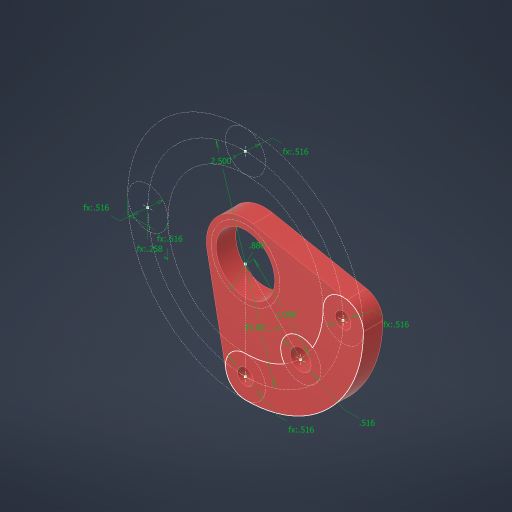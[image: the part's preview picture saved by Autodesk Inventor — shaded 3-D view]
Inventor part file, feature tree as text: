
AUTODESK INVENTOR PART (.ipt)
format: ipt  version: 2023.4 (Build 274418000, 418)  size: 238,080 bytes
history: native  units: in
note: dims shown in document units (in); Inventor stores cm internally (conversion verified against a paired STEP export)
features: sketch x2, extrude x2, hole x2, projected_geometry x1
ambient origin geometry x8: Origin, YZ Plane, XZ Plane, XY Plane, X Axis, Y Axis, Z Axis, Center Point
bodies: Solid1 (feature_tree)
feature tree (7):
  sketch  "Sketch1"  dims[d0=2.5in d1=0.88in]
  extrude  "Extrusion1"  Depth=0.88in
  hole  "Hole1"  [1 undecoded]
  extrude  "Extrusion2"  Depth=0.375in
  hole  "Hole2"  [1 undecoded]
  sketch  "Sketch2"  dims[d3=1.0in d4=45.0deg d5=0.5157in d6=0.5157in d7=0.5157in d8=0.5157in d9=0.5157in d10=0.2579in d11=0.5157in d12=0.25in d13=0.0in d14=0.2657in d15=0.38in d16=0.119in d17=0.25in d18=0.5635in d19=0.375in d20=0.0in d23=0.125in d24=0.75in d25=0.25in d26=0.0in d27=0.201in d28=0.75in d29=0.385in d30=0.25in d31=0.5635in d32=0.375in d33=0.0in]
  projected_geometry  "Project Cut Edges1"
note: 2 required parameter values undecoded (feature->parameter linkage not recoverable at this tier; creation-order binding heuristic only, values carry confidence <= 0.55)
